# Revit family: Langley Curve Wall Hung WC CHWC121-purged
name_source: partatom
category: Generic Models
revit_build: Autodesk Revit 2015 (Build: 20140606_1530(x64)
units: mm (PartAtom-declared; Revit-internal decimal feet)

## types (1)
- Langley Curve Wall Hung WC CHWC121-purged
    BIMobject category = Toilets
    BIMobject category code = sanitary-toilets
    BIMobject main category = sanitary
    BIMobjectmain category code = sanitary
    Brand url = www.theswc.co.uk
    Date of publishing = 1/6/2019
    Default Elevation = 1219 mm
    Description = Langley Curve rimless wall hung WC pan with hidden fixation, standard projection and horizontal outlet
    IFC Classification = Sanitary Terminal
    Manufacturer = The Sanitaryware Company
    Manufacturer Country = United Arab Emirates
    Manufacturer Name = The Sanitaryware Company
    Material = Ceramics - The Sanitaryware Company- Alpine White
    Model = CHWC121
    NBS Reference Description = WC Systems
    Nominal height = 430mm
    Nominal width = 360mm
    Product Family = Langley
    Product Group = Toilets
    Product SKU = Langley Curve Wall Hung WC, CHWC121
    Product certification = www.theswc.co.uk
    Uniclass 2.0 Description = WC Systems
    Weight Net(kg) = 29

## geometry (parser evidence)
native form markers: Sweep x3
no freeform markers — native parametric forms only
